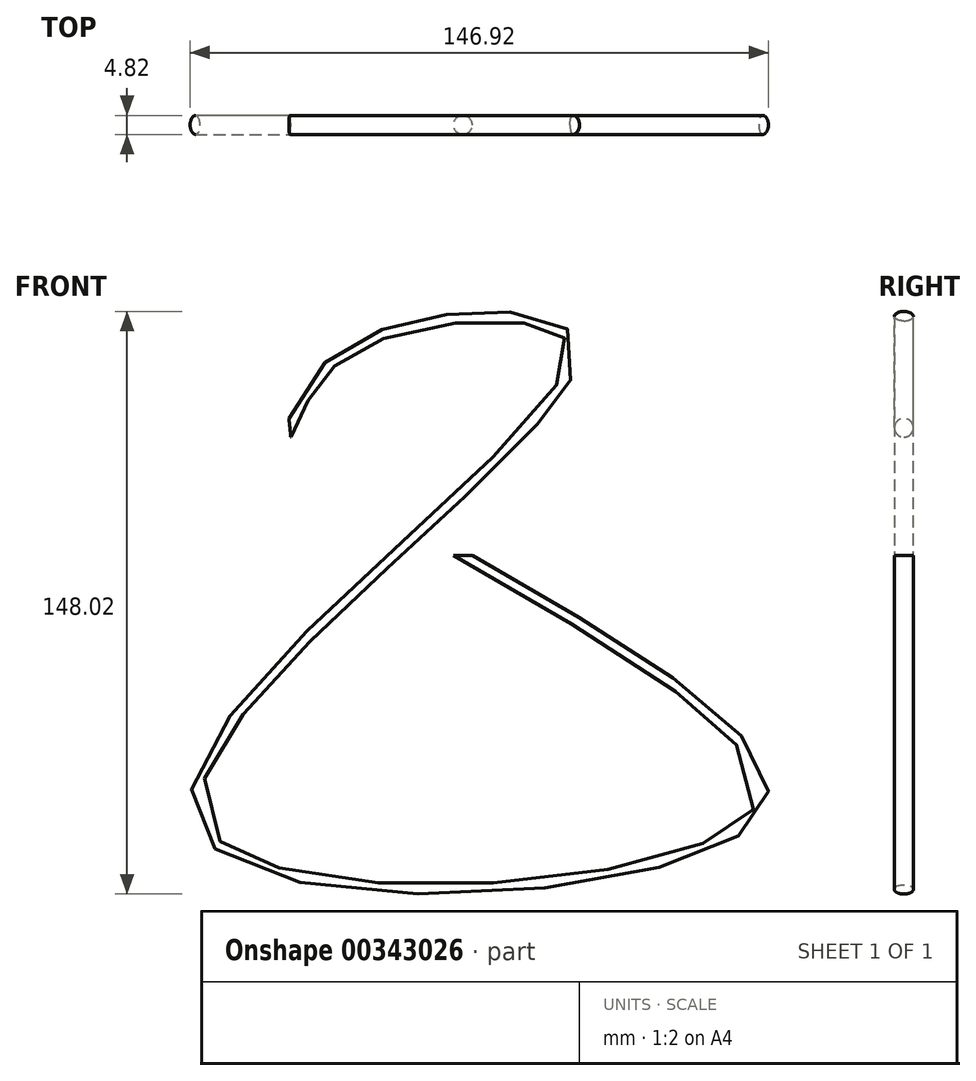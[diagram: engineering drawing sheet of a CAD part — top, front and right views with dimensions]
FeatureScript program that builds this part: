
annotation { "Feature Type Name" : "Feature", "Feature Type Description" : "" }
export const myFeature = defineFeature(function(context is Context, id is Id, definition is map)
    precondition{}
    {
        {
            var Q0;
            Q0=qCreatedBy(makeId("Front.planeOp"),FACE);
            var sketch = newSketch(context, id + "F0", { "sketchPlane" : qUnion([Q0])});
            skFitSpline(sketch, "E0", {"points": [v(-43.94, 32.44) * mm, v(-22.14, 55.54) * mm, v(28.15, 51) * mm, v(-67.47, -66.2) * mm, v(72.19, -67.93) * mm, v(0, 0) * mm], "startDerivative": vector(98.4, 219.76) * mm, "endDerivative": vector(-636.34, 363.03) * mm});
            skSolve(sketch);
        }
        {
            var Q0;
            Q0=qCreatedBy(makeId("Top.planeOp"),FACE);
            var sketch = newSketch(context, id + "F1", { "sketchPlane" : qUnion([Q0])});
            skCircle(sketch, "E1", {"center": v(0, 0) * mm, "radius": 2.41 * mm});
            skSolve(sketch);
        }
        {
            var Q0;
            Q0=makeQuery(id+"F1.imprint","IMPRINT",FACE,{"disambiguationData":[TD([[makeQuery(id+"F1.imprint","IMPRINT",EDGE,{"derivedFrom":sQuery(id+"F1.wireOp",EDGE,"E1")}),1.0]])]});
            var Q1;
            Q1=sQuery(id+"F0.wireOp",EDGE,"E0");
            sweep(context, id + "F2", {"profiles" : qUnion([Q0]), "path" : qUnion([Q1])});
        }
    });
